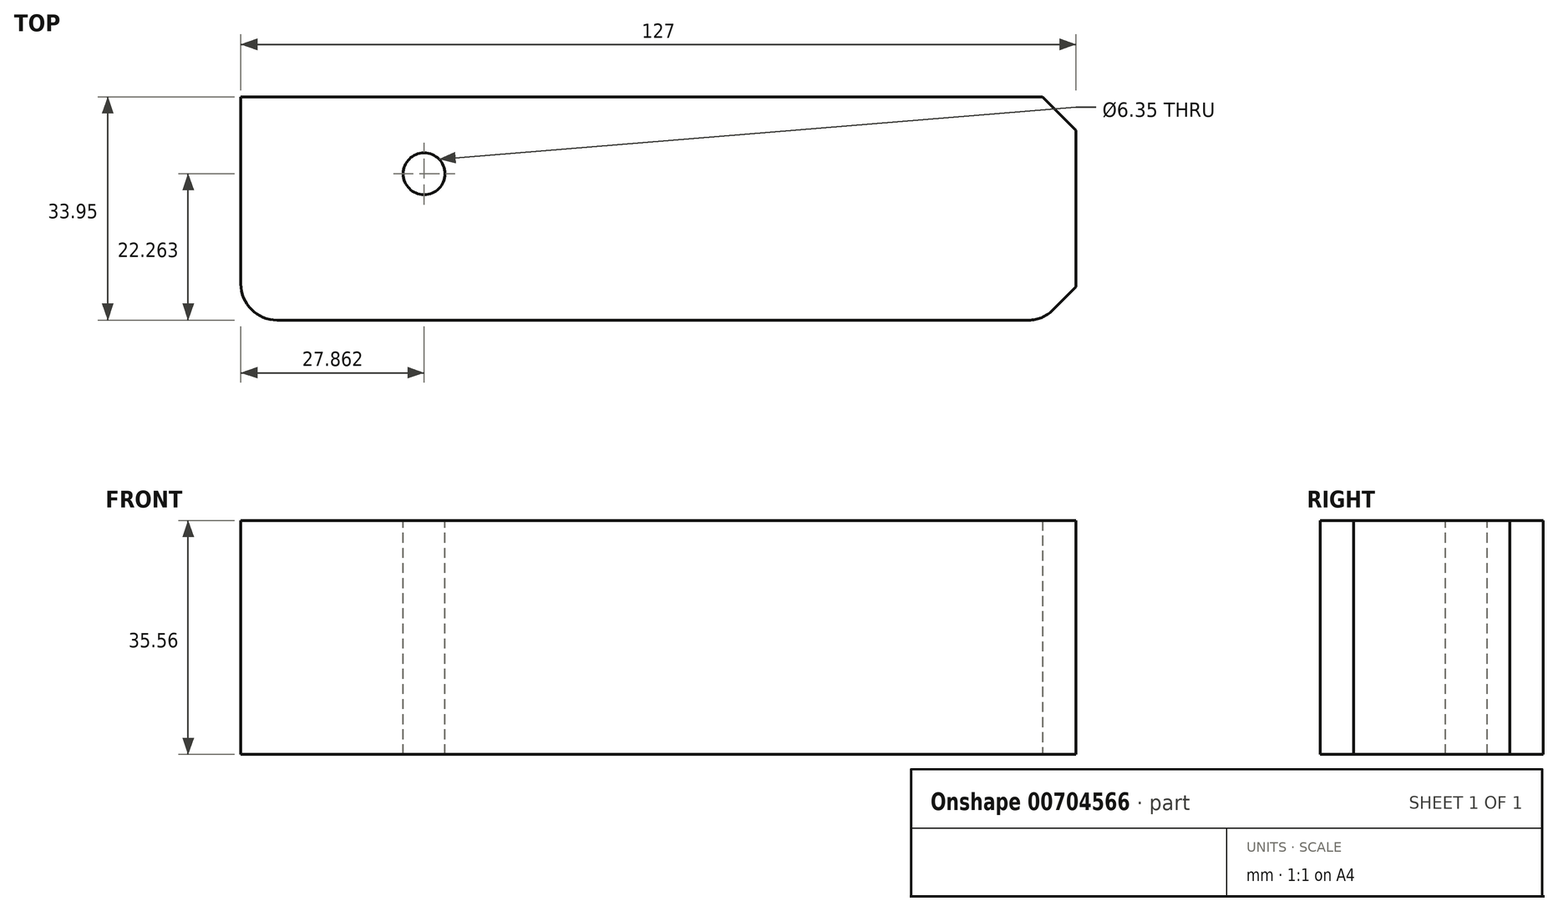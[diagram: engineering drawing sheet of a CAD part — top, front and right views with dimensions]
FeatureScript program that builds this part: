
annotation { "Feature Type Name" : "Feature", "Feature Type Description" : "" }
export const myFeature = defineFeature(function(context is Context, id is Id, definition is map)
    precondition{}
    {
        {
            var Q0;
            Q0=qCreatedBy(makeId("Top.planeOp"),FACE);
            var sketch = newSketch(context, id + "F0", { "sketchPlane" : qUnion([Q0])});
            skLineSegment(sketch, "E0.bottom", {"start": v(0, 0) * mm, "end": v(127, 0) * mm});
            skLineSegment(sketch, "E0.top", {"start": v(0, -33.95) * mm, "end": v(127, -33.95) * mm});
            skLineSegment(sketch, "E0.left", {"start": v(0, 0) * mm, "end": v(0, -33.95) * mm});
            skLineSegment(sketch, "E0.right", {"start": v(127, 0) * mm, "end": v(127, -33.95) * mm});
            skSolve(sketch);
        }
        {
            var Q0;
            Q0=makeQuery(id+"F0.imprint","IMPRINT",FACE,{"disambiguationData":[TD([[makeQuery(id+"F0.imprint","IMPRINT",EDGE,{"derivedFrom":sQuery(id+"F0.wireOp",EDGE,"E0.bottom")}),-1.0]])]});
            extrude(context, id + "F1", {"entities" : qUnion([Q0]), "depth" : 35.56 * mm, "offsetDistance" : 25.4 * mm});
        }
        {
            var Q0;
            Q0=makeQuery(id+"F1.opExtrude","SWEPT_EDGE",EDGE,{"disambiguationData":[OSD([sQuery(id+"F0.wireOp",EDGE,"E0.top"),sQuery(id+"F0.wireOp",EDGE,"E0.left")])]});
            fillet(context, id + "F2", {"entities" : qUnion([Q0]), "radius" : 5.52 * mm, "tangentPropagation" : true, "allowEdgeOverflow" : false});
        }
        {
            var Q0;
            Q0=makeQuery(id+"F1.opExtrude","SWEPT_EDGE",EDGE,{"disambiguationData":[OSD([sQuery(id+"F0.wireOp",EDGE,"E0.top"),sQuery(id+"F0.wireOp",EDGE,"E0.right")])]});
            chamfer(context, id + "F3", {"entities" : qUnion([Q0]), "width" : 5.08 * mm, "tangentPropagation" : true});
        }
        {
            var Q0;
            Q0=makeQuery(id+"F1.opExtrude","CAP_FACE",FACE,{"disambiguationData":[OSD([sQuery(id+"F0.wireOp",EDGE,"E0.bottom"),sQuery(id+"F0.wireOp",EDGE,"E0.top"),sQuery(id+"F0.wireOp",EDGE,"E0.left"),sQuery(id+"F0.wireOp",EDGE,"E0.right")])],"isStart":false});
            var sketch = newSketch(context, id + "F4", { "sketchPlane" : qUnion([Q0])});
            skPoint(sketch, "E1", {"position": v(27.86, -11.69) * mm});
            skPoint(sketch, "E2", {"position": v(46.04, -11.98) * mm});
            skSolve(sketch);
        }
        {
            var Q0;
            Q0=sQuery(id+"F4.wireOp",VERTEX,"E1");
            var Q1;
            Q1=makeQuery(id+"F1.opExtrude","SWEPT_BODY",BODY,{"disambiguationData":[OSD([sQuery(id+"F0.wireOp",EDGE,"E0.bottom"),sQuery(id+"F0.wireOp",EDGE,"E0.top"),sQuery(id+"F0.wireOp",EDGE,"E0.left"),sQuery(id+"F0.wireOp",EDGE,"E0.right")])]});
            hole(context, id + "F5", {"style" : HoleStyle.SIMPLE, "endStyle" : HoleEndStyle.THROUGH, "holeDiameter" : 6.35 * mm, "majorDiameter" : 6.35 * mm, "isTappedThrough" : true, "tappedDepth" : 12.7 * mm, "tapClearance" : 3, "locations" : qUnion([Q0]), "scope" : qUnion([Q1])});
        }
        {
            var Q0;
            {var subQ0=sQuery(id+"F0.wireOp",EDGE,"E0.top");Q0=makeQuery(id+"F3.opChamfer","BLEND_EDGE",EDGE,{"blendedFrom":[makeQuery(id+"F1.opExtrude","SWEPT_EDGE",EDGE,{"disambiguationData":[OSD([subQ0,sQuery(id+"F0.wireOp",EDGE,"E0.right")])]}),makeQuery(id+"F1.opExtrude","SWEPT_FACE",FACE,{"disambiguationData":[OSD([subQ0])]})],"blendedInto":[makeQuery(id+"F1.opExtrude","SWEPT_FACE",FACE,{"disambiguationData":[OSD([subQ0])]})]});}
            fillet(context, id + "F6", {"entities" : qUnion([Q0]), "radius" : 5.08 * mm, "tangentPropagation" : true, "allowEdgeOverflow" : false});
        }
        {
            var Q0;
            Q0=makeQuery(id+"F1.opExtrude","SWEPT_EDGE",EDGE,{"disambiguationData":[OSD([sQuery(id+"F0.wireOp",EDGE,"E0.bottom"),sQuery(id+"F0.wireOp",EDGE,"E0.right")])]});
            chamfer(context, id + "F7", {"entities" : qUnion([Q0]), "width" : 5.08 * mm, "tangentPropagation" : true});
        }
    });
